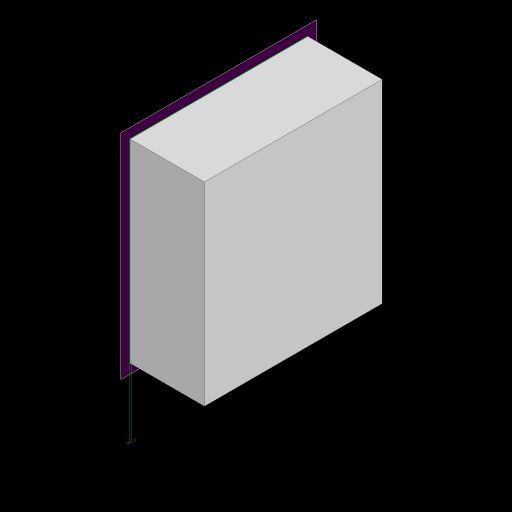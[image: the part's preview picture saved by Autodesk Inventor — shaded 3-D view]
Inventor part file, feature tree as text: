
AUTODESK INVENTOR PART (.ipt)
format: ipt  version: 2023 (Build 270158000, 158)  size: 289,792 bytes
history: native  units: in
note: dims shown in document units (in); Inventor stores cm internally (conversion verified against a paired STEP export)
features: sketch x10, extrude x9, projected_geometry x5, plane x2, fillet x2, split x1
ambient origin geometry x8: Origin, YZ Plane, XZ Plane, XY Plane, X Axis, Y Axis, Z Axis, Center Point
bodies: Solid1 (feature_tree)
feature tree (29):
  extrude  "Extrusion1"  Depth=3.937in
  sketch  "Sketch2"  dims[d2=5.1181in d3=0.0in d4=0.315in d5=0.0in]
  extrude  "Extrusion2"  Depth=0.315in TaperAngle=0.0deg
  extrude  "Extrusion3"  Depth=3.937in
  plane  "Work Plane1"
  extrude  "Extrusion4"  Depth=5.1181in
  fillet  "Fillet1"  Radius=5.1181in
  sketch  "Sketch8"  dims[d8=1.9685in d9=2.5591in d10=5.1181in]
  extrude  "Extrusion10"  Depth=0.1496in
  extrude  "Extrusion11"  [1 undecoded]
  fillet  "Fillet2"  Radius=0.1969in
  extrude  "Extrusion12"  Depth=0.1969in
  extrude  "Extrusion13"  Depth=3.5433in TaperAngle=0.0deg
  extrude  "Extrusion14"  Depth=0.1969in TaperAngle=0.0deg
  plane  "Work Plane2"
  split  "Split1"
  sketch  "Sketch18"  dims[d82=4.685in d84=5.0in d85=0.0in d86=0.1969in d87=45.0deg d88=45.0deg d90=45.0deg d91=45.0deg d92=0.7874in d93=0.9843in d94=0.7874in d95=0.9843in d96=0.0394in d97=3.3465in d98=4.3307in d99=3.5433in d100=0.0984in d101=0.1575in d102=0.1693in d103=0.1417in d104=0.1969in d105=0.1693in d107=4.7244in d108=0.1969in d109=0.1575in d110=0.1417in d111=0.1969in d112=0.1417in d113=0.1969in d114=0.1417in d115=0.1969in d116=0.1181in d117=0.0in d118=0.7087in d119=0.1181in d121=0.7087in d122=1.3386in d123=0.7874in d124=0.0in d125=45.0deg d126=2.874in d129=3.5433in d130=0.1673in d131=0.1417in d135=0.1417in d136=0.1417in d137=0.1417in d138=1.5748in d139=0.0in d140=0.0512in]
  sketch  "Sketch1"  dims[d0=4.685in d1=3.937in]
  sketch  "Sketch3"  dims[d6=3.5433in d7=3.937in]
  projected_geometry  "Projected Loop1"
  sketch  "Sketch10"  dims[d11=2.874in d12=0.1496in]
  projected_geometry  "Projected Loop2"
  sketch  "Sketch12"  dims[d13=0.7087in d14=0.0in d15=-0.1969in d16=0.1969in]
  projected_geometry  "Projected Loop4"
  sketch  "Sketch13"  dims[d17=0.1969in d18=0.1969in]
  sketch  "Sketch14"  dims[d19=3.5433in d20=0.0in d21=3.5433in d22=0.0in]
  sketch  "Sketch15"  dims[d23=0.1969in d74=0.1969in d75=0.0in]
  projected_geometry  "Projected Loop5"
  projected_geometry  "Project Cut Edges1"
note: 1 required parameter value undecoded (feature->parameter linkage not recoverable at this tier; creation-order binding heuristic only, values carry confidence <= 0.55)
